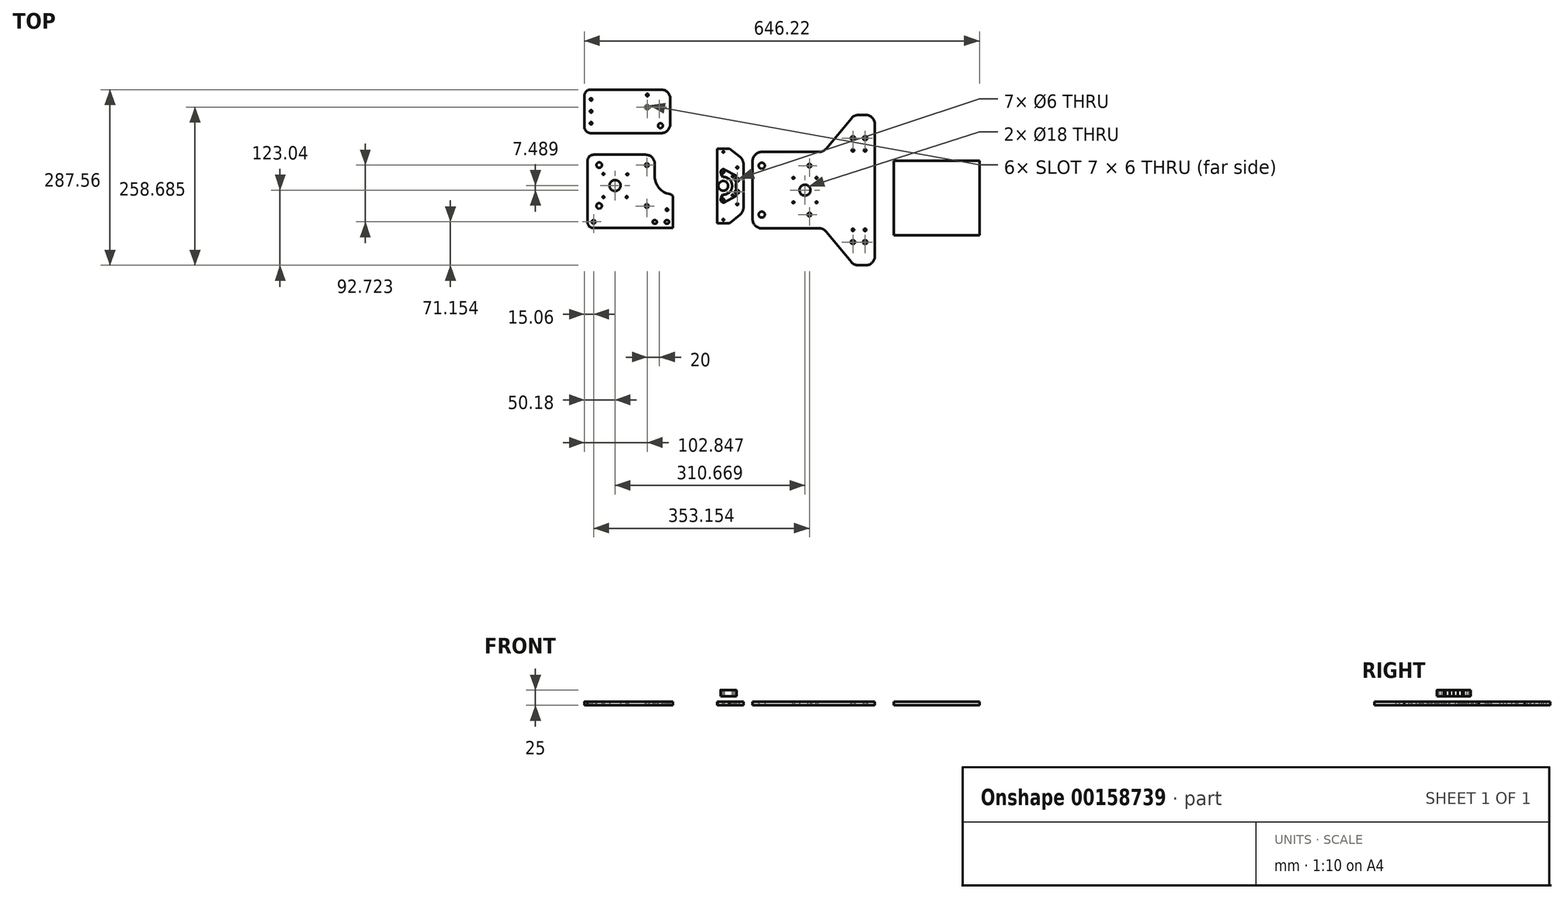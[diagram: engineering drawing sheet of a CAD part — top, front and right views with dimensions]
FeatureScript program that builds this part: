
annotation { "Feature Type Name" : "Feature", "Feature Type Description" : "" }
export const myFeature = defineFeature(function(context is Context, id is Id, definition is map)
    precondition{}
    {
        {
            var Q0;
            Q0=qCreatedBy(makeId("Top.planeOp"),FACE);
            var sketch = newSketch(context, id + "F0", { "sketchPlane" : qUnion([Q0])});
            skLineSegment(sketch, "E0", {"start": v(-213.09, -52.09) * mm, "end": v(-207.09, -52.1) * mm, "construction": true});
            skLineSegment(sketch, "E1", {"start": v(-193.09, -52.12) * mm, "end": v(-187.09, -52.13) * mm, "construction": true});
            skCircle(sketch, "E2", {"center": v(-210.09, -52.1) * mm, "radius": 3 * mm});
            skCircle(sketch, "E3", {"center": v(-190.09, -52.13) * mm, "radius": 3 * mm});
            skLineSegment(sketch, "E4", {"start": v(-207.09, -52.1) * mm, "end": v(-193.09, -52.12) * mm, "construction": true});
            skLineSegment(sketch, "E5.bottom", {"start": v(-180.09, -62.11) * mm, "end": v(-220.09, -62.11) * mm});
            skLineSegment(sketch, "E5.top", {"start": v(-180.09, -42.11) * mm, "end": v(-220.09, -42.11) * mm, "construction": true});
            skLineSegment(sketch, "E5.left", {"start": v(-180.09, -62.11) * mm, "end": v(-180.09, -42.11) * mm});
            skLineSegment(sketch, "E5.right", {"start": v(-220.09, -62.11) * mm, "end": v(-220.09, -42.11) * mm, "construction": true});
            skPoint(sketch, "E5.middle", {"position": v(-200.09, -52.11) * mm});
            skPoint(sketch, "E6", {"position": v(-320.09, 57.89) * mm});
            skLineSegment(sketch, "E7.bottom", {"start": v(-180.09, -62.11) * mm, "end": v(-310.09, -62.11) * mm});
            skLineSegment(sketch, "E7.top", {"start": v(-225.09, 57.89) * mm, "end": v(-310.09, 57.89) * mm});
            skLineSegment(sketch, "E7.left", {"start": v(-180.09, -62.11) * mm, "end": v(-180.09, -11.76) * mm});
            skLineSegment(sketch, "E7.right", {"start": v(-320.09, -52.11) * mm, "end": v(-320.09, 47.89) * mm});
            skLineSegment(sketch, "E8", {"start": v(-283.97, 7.5) * mm, "end": v(-265.9, 7.47) * mm, "construction": true});
            skCircle(sketch, "E9", {"center": v(-274.94, 7.49) * mm, "radius": 9 * mm});
            skLineSegment(sketch, "E10", {"start": v(-305.53, -25.87) * mm, "end": v(-296.53, -25.93) * mm, "construction": true});
            skCircle(sketch, "E11", {"center": v(-301.03, -25.9) * mm, "radius": 4.5 * mm});
            skLineSegment(sketch, "E12", {"start": v(-226, -26.03) * mm, "end": v(-220, -26.03) * mm, "construction": true});
            skCircle(sketch, "E13", {"center": v(-223, -26.03) * mm, "radius": 3 * mm});
            skCircle(sketch, "E14.MirrorC", {"center": v(-300.93, 40.96) * mm, "radius": 4.5 * mm});
            skCircle(sketch, "E15.MirrorC", {"center": v(-222.9, 40.84) * mm, "radius": 3 * mm});
            skLineSegment(sketch, "E16", {"start": v(-192.07, -32.1) * mm, "end": v(-188.07, -32.1) * mm, "construction": true});
            skLineSegment(sketch, "E17", {"start": v(-313.06, -51.89) * mm, "end": v(-307.06, -51.89) * mm, "construction": true});
            skCircle(sketch, "E18", {"center": v(-310.06, -51.89) * mm, "radius": 3 * mm});
            skCircle(sketch, "E19", {"center": v(-190.07, -32.1) * mm, "radius": 2 * mm});
            skLineSegment(sketch, "E20", {"start": v(-210.09, 42.89) * mm, "end": v(-210.09, 22.89) * mm});
            skLineSegment(sketch, "E21", {"start": v(-184.91, -6.72) * mm, "end": v(-184.28, -6.82) * mm});
            skArc(sketch, "E22.filletArc", {"start": v(-210.09, 42.89) * mm, "mid": v(-214.48, 53.5) * mm, "end": v(-225.09, 57.89) * mm});
            skPoint(sketch, "E23.visualSharp", {"position": v(-210.09, -2.62) * mm});
            skArc(sketch, "E23.filletArc", {"start": v(-210.09, 22.89) * mm, "mid": v(-202.94, 3.46) * mm, "end": v(-184.91, -6.72) * mm});
            skArc(sketch, "E24.filletArc", {"start": v(-180.09, -11.76) * mm, "mid": v(-181.28, -8.52) * mm, "end": v(-184.28, -6.82) * mm});
            skArc(sketch, "E25.filletArc", {"start": v(-310.09, 57.89) * mm, "mid": v(-317.16, 54.96) * mm, "end": v(-320.09, 47.89) * mm});
            skPoint(sketch, "E26.visualSharp", {"position": v(-320.09, -62.11) * mm});
            skArc(sketch, "E26.filletArc", {"start": v(-320.09, -52.11) * mm, "mid": v(-317.16, -59.18) * mm, "end": v(-310.09, -62.11) * mm});
            skLineSegment(sketch, "E27", {"start": v(-314.12, 164.52) * mm, "end": v(-314.12, 128.92) * mm, "construction": true});
            skLineSegment(sketch, "E28.bottom", {"start": v(-199.64, 93.32) * mm, "end": v(-315.12, 93.32) * mm});
            skLineSegment(sketch, "E28.top", {"start": v(-199.64, 164.52) * mm, "end": v(-315.12, 164.52) * mm});
            skLineSegment(sketch, "E28.left", {"start": v(-184.64, 108.32) * mm, "end": v(-184.64, 149.52) * mm});
            skLineSegment(sketch, "E28.right", {"start": v(-325.12, 103.32) * mm, "end": v(-325.12, 154.52) * mm});
            skCircle(sketch, "E29", {"center": v(-314.12, 128.92) * mm, "radius": 2 * mm});
            skLineSegment(sketch, "E30", {"start": v(-314.12, 128.92) * mm, "end": v(-314.12, 93.32) * mm, "construction": true});
            skCircle(sketch, "E31", {"center": v(-314.12, 109.4) * mm, "radius": 2 * mm});
            skLineSegment(sketch, "E32", {"start": v(-314.12, 128.92) * mm, "end": v(-312.12, 128.92) * mm, "construction": true});
            skPoint(sketch, "E33.orphan", {"position": v(-166.44, 128.92) * mm});
            skPoint(sketch, "E34", {"position": v(-222.27, 135.65) * mm});
            skPoint(sketch, "E35", {"position": v(-202.27, 135.62) * mm});
            skCircle(sketch, "E36", {"center": v(-222.27, 135.65) * mm, "radius": 2.5 * mm});
            skCircle(sketch, "E37", {"center": v(-202.27, 135.62) * mm, "radius": 2.5 * mm});
            skCircle(sketch, "E38.MirrorC", {"center": v(-314.12, 148.45) * mm, "radius": 2 * mm});
            skLineSegment(sketch, "E39.bottom", {"start": v(-209.59, -49.1) * mm, "end": v(-210.59, -49.1) * mm});
            skLineSegment(sketch, "E39.top", {"start": v(-209.59, -55.1) * mm, "end": v(-210.59, -55.1) * mm});
            skLineSegment(sketch, "E39.left", {"start": v(-209.59, -49.1) * mm, "end": v(-209.59, -55.1) * mm});
            skLineSegment(sketch, "E39.right", {"start": v(-210.59, -49.1) * mm, "end": v(-210.59, -55.1) * mm});
            skArc(sketch, "E40", {"start": v(-209.59, -55.1) * mm, "mid": v(-206.59, -52.1) * mm, "end": v(-209.59, -49.1) * mm});
            skArc(sketch, "E41", {"start": v(-210.59, -49.1) * mm, "mid": v(-213.59, -52.1) * mm, "end": v(-210.59, -55.1) * mm});
            skLineSegment(sketch, "E42", {"start": v(-200.09, -52.11) * mm, "end": v(-200.09, -47.54) * mm, "construction": true});
            skArc(sketch, "E43.MirrorCS", {"start": v(-190.59, -55.1) * mm, "mid": v(-193.59, -52.1) * mm, "end": v(-190.59, -49.1) * mm});
            skArc(sketch, "E44.MirrorCS", {"start": v(-189.59, -49.1) * mm, "mid": v(-186.59, -52.1) * mm, "end": v(-189.59, -55.1) * mm});
            skLineSegment(sketch, "E45.MirrorCS", {"start": v(-190.59, -55.1) * mm, "end": v(-189.59, -55.1) * mm});
            skLineSegment(sketch, "E46.MirrorCS", {"start": v(-190.59, -49.1) * mm, "end": v(-189.59, -49.1) * mm});
            skLineSegment(sketch, "E47", {"start": v(-222.27, 128.92) * mm, "end": v(-202.27, 135.62) * mm, "construction": true});
            skLineSegment(sketch, "E48", {"start": v(-202.27, 135.62) * mm, "end": v(-202.27, 128.92) * mm, "construction": true});
            skLineSegment(sketch, "E49", {"start": v(-202.27, 128.92) * mm, "end": v(-202.27, 128.92) * mm});
            skCircle(sketch, "E50", {"center": v(-222.1, 155.65) * mm, "radius": 2 * mm});
            skLineSegment(sketch, "E51", {"start": v(-204.73, 105.5) * mm, "end": v(-196.73, 105.42) * mm, "construction": true});
            skCircle(sketch, "E52", {"center": v(-200.73, 105.46) * mm, "radius": 4 * mm});
            skLineSegment(sketch, "E53.trimOffspring", {"start": v(-222.27, 128.92) * mm, "end": v(-202.27, 128.92) * mm, "construction": true});
            skPoint(sketch, "E54.orphan", {"position": v(-184.64, 128.92) * mm});
            skLineSegment(sketch, "E55", {"start": v(-212.27, 128.92) * mm, "end": v(-212.27, 142.55) * mm, "construction": true});
            skLineSegment(sketch, "E56.bottom", {"start": v(-222.77, 138.65) * mm, "end": v(-221.77, 138.65) * mm});
            skLineSegment(sketch, "E56.top", {"start": v(-222.77, 132.65) * mm, "end": v(-221.77, 132.65) * mm});
            skLineSegment(sketch, "E56.left", {"start": v(-222.77, 138.65) * mm, "end": v(-222.77, 132.65) * mm});
            skLineSegment(sketch, "E56.right", {"start": v(-221.77, 138.65) * mm, "end": v(-221.77, 132.65) * mm});
            skArc(sketch, "E57", {"start": v(-221.77, 132.65) * mm, "mid": v(-218.77, 135.65) * mm, "end": v(-221.77, 138.65) * mm});
            skArc(sketch, "E58", {"start": v(-222.77, 138.65) * mm, "mid": v(-225.77, 135.65) * mm, "end": v(-222.77, 132.65) * mm});
            skArc(sketch, "E59.MirrorCS", {"start": v(-202.77, 132.65) * mm, "mid": v(-205.77, 135.65) * mm, "end": v(-202.77, 138.65) * mm});
            skLineSegment(sketch, "E60.MirrorCS", {"start": v(-202.27, 135.65) * mm, "end": v(-202.27, 128.92) * mm, "construction": true});
            skArc(sketch, "E61.MirrorCS", {"start": v(-201.77, 138.65) * mm, "mid": v(-198.77, 135.65) * mm, "end": v(-201.77, 132.65) * mm});
            skLineSegment(sketch, "E62.MirrorCS", {"start": v(-201.77, 132.65) * mm, "end": v(-202.77, 132.65) * mm});
            skLineSegment(sketch, "E63", {"start": v(-201.77, 138.65) * mm, "end": v(-202.77, 138.65) * mm});
            skPoint(sketch, "E64.visualSharp", {"position": v(-184.64, 164.52) * mm});
            skArc(sketch, "E64.filletArc", {"start": v(-184.64, 149.52) * mm, "mid": v(-189.03, 160.13) * mm, "end": v(-199.64, 164.52) * mm});
            skPoint(sketch, "E65.visualSharp", {"position": v(-184.64, 93.32) * mm});
            skArc(sketch, "E65.filletArc", {"start": v(-199.64, 93.32) * mm, "mid": v(-189.03, 97.71) * mm, "end": v(-184.64, 108.32) * mm});
            skPoint(sketch, "E66.visualSharp", {"position": v(-325.12, 164.52) * mm});
            skArc(sketch, "E66.filletArc", {"start": v(-315.12, 164.52) * mm, "mid": v(-322.19, 161.6) * mm, "end": v(-325.12, 154.52) * mm});
            skPoint(sketch, "E67.visualSharp", {"position": v(-325.12, 93.32) * mm});
            skArc(sketch, "E67.filletArc", {"start": v(-325.12, 103.32) * mm, "mid": v(-322.19, 96.25) * mm, "end": v(-315.12, 93.32) * mm});
            skLineSegment(sketch, "E68.bottom", {"start": v(-255.94, 26.49) * mm, "end": v(-293.94, 26.49) * mm, "construction": true});
            skLineSegment(sketch, "E68.top", {"start": v(-255.94, -11.51) * mm, "end": v(-293.94, -11.51) * mm, "construction": true});
            skLineSegment(sketch, "E68.left", {"start": v(-255.94, 26.49) * mm, "end": v(-255.94, -11.51) * mm, "construction": true});
            skLineSegment(sketch, "E68.right", {"start": v(-293.94, 26.49) * mm, "end": v(-293.94, -11.51) * mm, "construction": true});
            skCircle(sketch, "E69", {"center": v(-293.94, -11.51) * mm, "radius": 1.5 * mm});
            skCircle(sketch, "E70", {"center": v(-293.94, 26.49) * mm, "radius": 1.5 * mm});
            skCircle(sketch, "E71", {"center": v(-254.75, 25.88) * mm, "radius": 1.5 * mm});
            skCircle(sketch, "E72", {"center": v(-255.94, -11.51) * mm, "radius": 1.5 * mm});
            skSolve(sketch);
        }
        {
            var Q0;
            Q0=qCreatedBy(makeId("Top.planeOp"),FACE);
            var sketch = newSketch(context, id + "F1", { "sketchPlane" : qUnion([Q0])});
            skLineSegment(sketch, "E73", {"start": v(-64.93, -28.37) * mm, "end": v(-64.93, 7) * mm});
            skLineSegment(sketch, "E74", {"start": v(-107.93, -54) * mm, "end": v(-87.93, -54) * mm});
            skLineSegment(sketch, "E75", {"start": v(120.27, -123) * mm, "end": v(150.07, -123) * mm, "construction": true});
            skLineSegment(sketch, "E76", {"start": v(150.07, -0.02) * mm, "end": v(150.07, 108) * mm});
            skLineSegment(sketch, "E77", {"start": v(111.57, 117.55) * mm, "end": v(70.66, 67.97) * mm});
            skLineSegment(sketch, "E78", {"start": v(-49.9, 62.51) * mm, "end": v(-49.9, 62.51) * mm});
            skLineSegment(sketch, "E79", {"start": v(-49.9, 47.51) * mm, "end": v(-49.91, 0) * mm});
            skLineSegment(sketch, "E80", {"start": v(194.1, 48.08) * mm, "end": v(181.1, 48.08) * mm});
            skLineSegment(sketch, "E81", {"start": v(150.07, -0.02) * mm, "end": v(-49.91, 0) * mm, "construction": true});
            skPoint(sketch, "E81.startSnap0", {"position": v(150.07, 0) * mm});
            skCircle(sketch, "E82", {"center": v(35.73, 0) * mm, "radius": 9 * mm});
            skCircle(sketch, "E83", {"center": v(-34.92, -39.99) * mm, "radius": 5 * mm});
            skPoint(sketch, "E84.orphan", {"position": v(68.45, -40.11) * mm});
            skCircle(sketch, "E85", {"center": v(43.08, -40.08) * mm, "radius": 3 * mm});
            skCircle(sketch, "E86.MirrorC", {"center": v(-34.9, 39.98) * mm, "radius": 5 * mm});
            skCircle(sketch, "E87.MirrorC", {"center": v(43.1, 40.06) * mm, "radius": 3 * mm});
            skCircle(sketch, "E88", {"center": v(114.07, -85.02) * mm, "radius": 3 * mm});
            skLineSegment(sketch, "E89", {"start": v(114.07, -85.02) * mm, "end": v(114.07, -65.02) * mm, "construction": true});
            skCircle(sketch, "E90", {"center": v(114.07, -65.02) * mm, "radius": 2 * mm});
            skLineSegment(sketch, "E91", {"start": v(114.07, -85.02) * mm, "end": v(134.07, -85.02) * mm, "construction": true});
            skLineSegment(sketch, "E92", {"start": v(124.07, -85.02) * mm, "end": v(124.07, -79.56) * mm, "construction": true});
            skCircle(sketch, "E93.MirrorC", {"center": v(134.07, -65.02) * mm, "radius": 2 * mm});
            skCircle(sketch, "E94.MirrorC", {"center": v(134.09, 64.98) * mm, "radius": 2 * mm});
            skLineSegment(sketch, "E95.MirrorCS", {"start": v(114.1, 84.99) * mm, "end": v(114.09, 64.99) * mm, "construction": true});
            skCircle(sketch, "E96.MirrorC", {"center": v(114.09, 64.99) * mm, "radius": 2 * mm});
            skLineSegment(sketch, "E97.bottom", {"start": v(54.73, 20) * mm, "end": v(16.73, 20) * mm, "construction": true});
            skLineSegment(sketch, "E97.top", {"start": v(54.73, -20) * mm, "end": v(16.73, -20) * mm, "construction": true});
            skLineSegment(sketch, "E97.left", {"start": v(54.73, 20) * mm, "end": v(54.73, -20) * mm, "construction": true});
            skLineSegment(sketch, "E97.right", {"start": v(16.73, 20) * mm, "end": v(16.73, -20) * mm, "construction": true});
            skCircle(sketch, "E98", {"center": v(16.73, 20) * mm, "radius": 1.5 * mm});
            skCircle(sketch, "E99", {"center": v(54.73, 20) * mm, "radius": 1.5 * mm});
            skCircle(sketch, "E100", {"center": v(54.73, -20) * mm, "radius": 1.5 * mm});
            skCircle(sketch, "E101", {"center": v(16.73, -20) * mm, "radius": 1.5 * mm});
            skLineSegment(sketch, "E102.bottom", {"start": v(144.07, -75.02) * mm, "end": v(104.07, -75.02) * mm, "construction": true});
            skLineSegment(sketch, "E102.top", {"start": v(144.07, -95.02) * mm, "end": v(104.07, -95.02) * mm, "construction": true});
            skLineSegment(sketch, "E102.left", {"start": v(144.07, -75.02) * mm, "end": v(144.07, -95.02) * mm, "construction": true});
            skLineSegment(sketch, "E102.right", {"start": v(104.07, -75.02) * mm, "end": v(104.07, -95.02) * mm, "construction": true});
            skPoint(sketch, "E102.middle", {"position": v(124.07, -85.02) * mm});
            skLineSegment(sketch, "E103", {"start": v(-105.92, 7) * mm, "end": v(-89.93, 7) * mm, "construction": true});
            skPoint(sketch, "E104.orphan", {"position": v(150.07, -123) * mm});
            skLineSegment(sketch, "E105", {"start": v(135.07, 123) * mm, "end": v(123.14, 123) * mm});
            skLineSegment(sketch, "E106", {"start": v(59.1, 62.51) * mm, "end": v(-34.9, 62.51) * mm});
            skPoint(sketch, "E107.visualSharp", {"position": v(-49.9, 62.51) * mm});
            skArc(sketch, "E107.filletArc", {"start": v(-34.9, 62.51) * mm, "mid": v(-45.51, 58.12) * mm, "end": v(-49.9, 47.51) * mm});
            skPoint(sketch, "E108.visualSharp", {"position": v(66.16, 62.51) * mm});
            skArc(sketch, "E108.filletArc", {"start": v(59.1, 62.51) * mm, "mid": v(65.49, 63.94) * mm, "end": v(70.66, 67.97) * mm});
            skPoint(sketch, "E109.visualSharp", {"position": v(116.07, 123) * mm});
            skArc(sketch, "E109.filletArc", {"start": v(123.14, 123) * mm, "mid": v(116.74, 121.57) * mm, "end": v(111.57, 117.55) * mm});
            skPoint(sketch, "E110.visualSharp", {"position": v(150.07, 123) * mm});
            skArc(sketch, "E110.filletArc", {"start": v(150.07, 108) * mm, "mid": v(145.68, 118.6) * mm, "end": v(135.07, 123) * mm});
            skLineSegment(sketch, "E111.MirrorCS", {"start": v(-49.92, -47.51) * mm, "end": v(-49.91, 0) * mm});
            skArc(sketch, "E112.MirrorCS", {"start": v(59.08, -62.54) * mm, "mid": v(65.47, -63.97) * mm, "end": v(70.65, -68) * mm});
            skLineSegment(sketch, "E113.MirrorCS", {"start": v(135.05, -123.04) * mm, "end": v(123.11, -123.04) * mm});
            skArc(sketch, "E114.MirrorCS", {"start": v(150.05, -108.04) * mm, "mid": v(145.66, -118.65) * mm, "end": v(135.05, -123.04) * mm});
            skLineSegment(sketch, "E115.MirrorCS", {"start": v(150.07, -0.02) * mm, "end": v(150.05, -108.04) * mm});
            skLineSegment(sketch, "E116.MirrorCS", {"start": v(111.54, -117.58) * mm, "end": v(70.65, -68) * mm});
            skArc(sketch, "E117.MirrorCS", {"start": v(123.11, -123.04) * mm, "mid": v(116.72, -121.6) * mm, "end": v(111.54, -117.58) * mm});
            skLineSegment(sketch, "E118.MirrorCS", {"start": v(59.08, -62.54) * mm, "end": v(-34.92, -62.52) * mm});
            skArc(sketch, "E119.MirrorCS", {"start": v(-34.92, -62.52) * mm, "mid": v(-45.53, -58.12) * mm, "end": v(-49.92, -47.51) * mm});
            skPoint(sketch, "E120.orphan", {"position": v(-64.93, 7) * mm});
            skPoint(sketch, "E121.orphan", {"position": v(-107.93, 7) * mm});
            skCircle(sketch, "E122", {"center": v(-97.92, 7) * mm, "radius": 8 * mm});
            skArc(sketch, "E123", {"start": v(-76.86, 0.38) * mm, "mid": v(-78.8, -3.26) * mm, "end": v(-76.46, -6.65) * mm});
            skLineSegment(sketch, "E124", {"start": v(-83.92, -8.5) * mm, "end": v(-80.92, -8.5) * mm});
            skCircle(sketch, "E125", {"center": v(-82.42, -8.5) * mm, "radius": 1.5 * mm});
            skLineSegment(sketch, "E126", {"start": v(-73.38, -23.41) * mm, "end": v(-76.47, -22.59) * mm});
            skCircle(sketch, "E127", {"center": v(-74.93, -23) * mm, "radius": 1.6 * mm});
            skLineSegment(sketch, "E128", {"start": v(-99.23, -48.5) * mm, "end": v(-96.63, -48.5) * mm});
            skCircle(sketch, "E129", {"center": v(-97.93, -48.5) * mm, "radius": 1.3 * mm});
            skLineSegment(sketch, "E130", {"start": v(-99.53, -15.5) * mm, "end": v(-96.33, -15.5) * mm});
            skCircle(sketch, "E131", {"center": v(-97.93, -15.5) * mm, "radius": 1.59 * mm});
            skPoint(sketch, "E132.orphan", {"position": v(-107.93, 68) * mm});
            skPoint(sketch, "E133.orphan", {"position": v(-64.93, 49.57) * mm});
            skPoint(sketch, "E134.end.orphan", {"position": v(-107.93, -54) * mm});
            skLineSegment(sketch, "E135", {"start": v(-107.93, 7) * mm, "end": v(-107.93, -54) * mm});
            skLineSegment(sketch, "E136", {"start": v(-87.93, -54) * mm, "end": v(-70.55, -40.08) * mm});
            skPoint(sketch, "E137.visualSharp", {"position": v(-64.93, -35.57) * mm});
            skArc(sketch, "E137.filletArc", {"start": v(-70.55, -40.08) * mm, "mid": v(-66.4, -34.86) * mm, "end": v(-64.93, -28.37) * mm});
            skArc(sketch, "E138", {"start": v(-98.23, -7.51) * mm, "mid": v(-87.77, -3.37) * mm, "end": v(-83.4, 7) * mm});
            skLineSegment(sketch, "E139", {"start": v(-97.92, 7) * mm, "end": v(-77.24, 7) * mm, "construction": true});
            skLineSegment(sketch, "E140", {"start": v(-76.31, -9.25) * mm, "end": v(-97.4, -20.38) * mm});
            skLineSegment(sketch, "E141", {"start": v(-101.48, -12.6) * mm, "end": v(-98.23, -7.51) * mm});
            skLineSegment(sketch, "E142", {"start": v(-76.31, -9.25) * mm, "end": v(-76.46, -6.65) * mm});
            skArc(sketch, "E143", {"start": v(-99.5, -19.77) * mm, "mid": v(-98.6, -20.15) * mm, "end": v(-97.65, -20.41) * mm});
            skCircle(sketch, "E144", {"center": v(-74.93, -2.98) * mm, "radius": 3 * mm});
            skLineSegment(sketch, "E145.trimOffspring", {"start": v(-76.86, 0.38) * mm, "end": v(-77.24, 7) * mm});
            skLineSegment(sketch, "E146.MirrorCS", {"start": v(-107.93, 7) * mm, "end": v(-107.93, 68) * mm});
            skLineSegment(sketch, "E147.MirrorCS", {"start": v(-107.93, 68) * mm, "end": v(-87.93, 68) * mm});
            skLineSegment(sketch, "E148.MirrorCS", {"start": v(-87.93, 68) * mm, "end": v(-70.55, 54.08) * mm});
            skArc(sketch, "E149.MirrorCS", {"start": v(-70.55, 54.08) * mm, "mid": v(-66.4, 48.86) * mm, "end": v(-64.93, 42.37) * mm});
            skLineSegment(sketch, "E150.MirrorCS", {"start": v(-64.93, 42.37) * mm, "end": v(-64.93, 7) * mm});
            skPoint(sketch, "E151.visualSharp", {"position": v(-103.32, -15.5) * mm});
            skArc(sketch, "E151.filletArc", {"start": v(-101.48, -12.6) * mm, "mid": v(-102.08, -16.63) * mm, "end": v(-99.5, -19.77) * mm});
            skArc(sketch, "E152.filletArc", {"start": v(-97.65, -20.41) * mm, "mid": v(-97.52, -20.42) * mm, "end": v(-97.4, -20.38) * mm});
            skLineSegment(sketch, "E153.MirrorCS", {"start": v(-76.31, 23.25) * mm, "end": v(-76.46, 20.65) * mm});
            skLineSegment(sketch, "E154.MirrorCS", {"start": v(-76.86, 13.62) * mm, "end": v(-77.24, 7) * mm});
            skArc(sketch, "E155.MirrorCS", {"start": v(-76.86, 13.62) * mm, "mid": v(-78.8, 17.26) * mm, "end": v(-76.46, 20.65) * mm});
            skArc(sketch, "E156.MirrorCS", {"start": v(-97.65, 34.41) * mm, "mid": v(-97.52, 34.42) * mm, "end": v(-97.4, 34.38) * mm});
            skArc(sketch, "E157.MirrorCS", {"start": v(-99.5, 33.77) * mm, "mid": v(-98.6, 34.15) * mm, "end": v(-97.65, 34.41) * mm});
            skLineSegment(sketch, "E158.MirrorCS", {"start": v(-101.48, 26.6) * mm, "end": v(-98.23, 21.51) * mm});
            skLineSegment(sketch, "E159.MirrorCS", {"start": v(-76.31, 23.25) * mm, "end": v(-97.4, 34.38) * mm});
            skArc(sketch, "E160.MirrorCS", {"start": v(-101.48, 26.6) * mm, "mid": v(-102.08, 30.63) * mm, "end": v(-99.5, 33.77) * mm});
            skArc(sketch, "E161.MirrorCS", {"start": v(-98.23, 21.51) * mm, "mid": v(-87.77, 17.37) * mm, "end": v(-83.4, 7) * mm});
            skCircle(sketch, "E162.MirrorC", {"center": v(-82.42, 22.5) * mm, "radius": 1.5 * mm});
            skCircle(sketch, "E163.MirrorC", {"center": v(-97.93, 29.5) * mm, "radius": 1.59 * mm});
            skCircle(sketch, "E164.MirrorC", {"center": v(-97.93, 62.5) * mm, "radius": 1.3 * mm});
            skCircle(sketch, "E165.MirrorC", {"center": v(-74.93, 37) * mm, "radius": 1.6 * mm});
            skCircle(sketch, "E166.MirrorC", {"center": v(-74.93, 16.98) * mm, "radius": 3 * mm});
            skLineSegment(sketch, "E167.bottom", {"start": v(114.57, -82.02) * mm, "end": v(113.57, -82.02) * mm});
            skLineSegment(sketch, "E167.top", {"start": v(114.57, -88.02) * mm, "end": v(113.57, -88.02) * mm});
            skLineSegment(sketch, "E167.left", {"start": v(114.57, -82.02) * mm, "end": v(114.57, -88.02) * mm});
            skLineSegment(sketch, "E167.right", {"start": v(113.57, -82.02) * mm, "end": v(113.57, -88.02) * mm});
            skArc(sketch, "E168", {"start": v(114.57, -88.02) * mm, "mid": v(117.57, -85.02) * mm, "end": v(114.57, -82.02) * mm});
            skArc(sketch, "E169", {"start": v(113.57, -82.02) * mm, "mid": v(110.57, -85.02) * mm, "end": v(113.57, -88.02) * mm});
            skArc(sketch, "E170.MirrorCS", {"start": v(134.57, -82.02) * mm, "mid": v(137.57, -85.02) * mm, "end": v(134.57, -88.02) * mm});
            skArc(sketch, "E171.MirrorCS", {"start": v(133.57, -88.02) * mm, "mid": v(130.57, -85.02) * mm, "end": v(133.57, -82.02) * mm});
            skLineSegment(sketch, "E172.MirrorCS", {"start": v(133.57, -82.02) * mm, "end": v(134.57, -82.02) * mm});
            skLineSegment(sketch, "E173.MirrorCS", {"start": v(133.57, -88.02) * mm, "end": v(134.57, -88.02) * mm});
            skLineSegment(sketch, "E174.MirrorCS", {"start": v(114.6, 81.98) * mm, "end": v(114.6, 87.98) * mm});
            skLineSegment(sketch, "E175.MirrorCS", {"start": v(114.6, 81.98) * mm, "end": v(113.6, 81.99) * mm});
            skLineSegment(sketch, "E176.MirrorCS", {"start": v(113.6, 81.99) * mm, "end": v(113.6, 87.99) * mm});
            skLineSegment(sketch, "E177.MirrorCS", {"start": v(114.6, 87.98) * mm, "end": v(113.6, 87.99) * mm});
            skLineSegment(sketch, "E178.MirrorCS", {"start": v(133.6, 87.98) * mm, "end": v(134.6, 87.98) * mm});
            skLineSegment(sketch, "E179.MirrorCS", {"start": v(133.6, 81.98) * mm, "end": v(134.6, 81.98) * mm});
            skArc(sketch, "E180.MirrorCS", {"start": v(113.6, 81.99) * mm, "mid": v(110.6, 84.99) * mm, "end": v(113.6, 87.99) * mm});
            skPoint(sketch, "E181.MirrorP", {"position": v(114.1, 84.99) * mm});
            skLineSegment(sketch, "E182.MirrorCS", {"start": v(124.1, 84.98) * mm, "end": v(124.1, 79.52) * mm, "construction": true});
            skPoint(sketch, "E183.MirrorP", {"position": v(124.1, 84.98) * mm});
            skCircle(sketch, "E184.MirrorC", {"center": v(114.1, 84.99) * mm, "radius": 3 * mm});
            skArc(sketch, "E185.MirrorCS", {"start": v(133.6, 87.98) * mm, "mid": v(130.6, 84.98) * mm, "end": v(133.6, 81.98) * mm});
            skArc(sketch, "E186.MirrorCS", {"start": v(134.6, 81.98) * mm, "mid": v(137.6, 84.98) * mm, "end": v(134.6, 87.98) * mm});
            skLineSegment(sketch, "E187.MirrorCS", {"start": v(114.1, 84.99) * mm, "end": v(134.1, 84.98) * mm, "construction": true});
            skArc(sketch, "E188.MirrorCS", {"start": v(114.6, 87.98) * mm, "mid": v(117.6, 84.98) * mm, "end": v(114.6, 81.98) * mm});
            skLineSegment(sketch, "E189.bottom", {"start": v(181.1, 48.08) * mm, "end": v(321.1, 48.08) * mm});
            skLineSegment(sketch, "E189.top", {"start": v(181.1, -73.92) * mm, "end": v(321.1, -73.92) * mm});
            skLineSegment(sketch, "E189.left", {"start": v(181.1, 48.08) * mm, "end": v(181.1, -73.92) * mm});
            skLineSegment(sketch, "E189.right", {"start": v(321.1, 48.08) * mm, "end": v(321.1, -73.92) * mm});
            skSolve(sketch);
        }
        {
            var Q0;
            Q0=makeQuery(id+"F1.imprint","IMPRINT",FACE,{"disambiguationData":[TD([[makeQuery(id+"F1.imprint","IMPRINT",EDGE,{"derivedFrom":sQuery(id+"F1.wireOp",EDGE,"E76")}),1.0]])]});
            var Q1;
            Q1=makeQuery(id+"F1.imprint","IMPRINT",FACE,{"disambiguationData":[TD([[makeQuery(id+"F1.imprint","IMPRINT",EDGE,{"derivedFrom":sQuery(id+"F1.wireOp",EDGE,"E73")}),1.0]])]});
            var Q2;
            Q2=makeQuery(id+"F1.imprint","IMPRINT",FACE,{"disambiguationData":[TD([[makeQuery(id+"F1.imprint","IMPRINT",EDGE,{"derivedFrom":sQuery(id+"F1.wireOp",EDGE,"E123")}),-1.0]])]});
            var Q3;
            Q3=makeQuery(id+"F1.imprint","IMPRINT",FACE,{"disambiguationData":[TD([[makeQuery(id+"F1.imprint","IMPRINT",EDGE,{"derivedFrom":sQuery(id+"F1.wireOp",EDGE,"E80")}),1.0]])]});
            var Q4;
            Q4=makeQuery(id+"F0.imprint","IMPRINT",FACE,{"disambiguationData":[TD([[makeQuery(id+"F0.imprint","IMPRINT",EDGE,{"derivedFrom":sQuery(id+"F0.wireOp",EDGE,"E2")}),-1.0]])]});
            var Q5;
            Q5=makeQuery(id+"F0.imprint","IMPRINT",FACE,{"disambiguationData":[TD([[makeQuery(id+"F0.imprint","IMPRINT",EDGE,{"derivedFrom":sQuery(id+"F0.wireOp",EDGE,"bbd79dd2-7b2a-41b3-a734-e22bc02ca5c2")}),1.0]])]});
            var Q6;
            Q6=makeQuery(id+"F0.imprint","IMPRINT",FACE,{"disambiguationData":[TD([[makeQuery(id+"F0.imprint","IMPRINT",EDGE,{"derivedFrom":sQuery(id+"F0.wireOp",EDGE,"E7.top")}),1.0]])]});
            var Q7;
            Q7=makeQuery(id+"F0.imprint","IMPRINT",FACE,{"disambiguationData":[TD([[makeQuery(id+"F0.imprint","IMPRINT",EDGE,{"derivedFrom":sQuery(id+"F0.wireOp",EDGE,"E28.bottom")}),-1.0]])]});
            var Q8;
            Q8=makeQuery(id+"F1.imprint","IMPRINT",FACE,{"disambiguationData":[TD([[makeQuery(id+"F1.imprint","IMPRINT",EDGE,{"derivedFrom":sQuery(id+"F1.wireOp",EDGE,"E189.top")}),1.0]])]});
            extrude(context, id + "F2", {"entities" : qUnion([Q0, Q1, Q2, Q3, Q4, Q5, Q6, Q7, Q8]), "depth" : 6 * mm});
        }
        {
            var Q0;
            Q0=makeQuery(id+"F1.imprint","IMPRINT",FACE,{"disambiguationData":[TD([[makeQuery(id+"F1.imprint","IMPRINT",EDGE,{"derivedFrom":sQuery(id+"F1.wireOp",EDGE,"E123")}),-1.0]])]});
            extrude(context, id + "F3", {"entities" : qUnion([Q0]), "depth" : 25 * mm, "hasSecondDirection" : true, "secondDirectionOppositeDirection" : false, "secondDirectionDepth" : 15 * mm});
        }
    });
